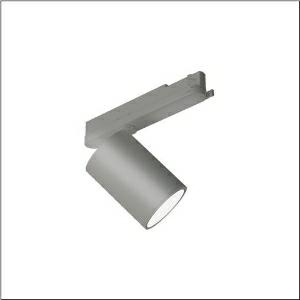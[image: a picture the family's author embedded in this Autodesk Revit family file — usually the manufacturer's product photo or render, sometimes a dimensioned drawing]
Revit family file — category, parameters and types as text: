
# Revit family: spot_31_51sf63mab4b
name_source: partatom
category: Lighting Fixtures
units: mm (PartAtom-declared; Revit-internal decimal feet)

## family parameters
Cut with Voids When Loaded = No
Host = Face
Light Source = No
Part Type = Normal
Room Calculation Point = No
Round Connector Dimension = Use Diameter
Shared = No

## types (1)
- --- (1 x LED, 5030 lm, 41.7 W, 3000K)
    Apparent Load = 42 VA
    CIE Flux Codes = 92 97 99 100 100
    Color Rendering = 90
    Color Temperature = 3000K
    Default Elevation = 1800 mm
    Description = Spot 31, directional spotlight, light control with lens, of PMMA, LED rated luminous flux: 4.830lm, light colour: 930, with 3-phase adapter, mains connection: 220..240V, AC, 50/60Hz, of aluminium, metallic grey (RAL 9006), length: 213mm, diameter: 90mm, protection rating (complete): IP20, insulation class (complete): insulation class I (protective earthing), certification: CE, impact resistance: IK02, permissible ambient temperature for indoor applications: -20..+40°C, packaging unit: 1 piece
    Height = 175 mm
    Lamp = 1 x LED
    Lamp Light Flux = 5030 lm
    Lamp Power = 41.7 W
    Lamp count = 1
    Length = 90 mm
    Luminous efficacy = 121 lm/W
    Manufacturer = Siteco
    ModVariant = No
    Model = 51SF63MAB4B
    Mounting Place = Ceiling
    Mounting Type = Pendant
    Number of Poles = 1
    OnlyDefault = Yes
    Power Factor = 1
    Product Name = Spot 31
    Product group = directional spotlight
    ProductGroupID = 906
    Protection Class = Protection class I
    Protection Degree = IP 20
    RLX_Detail_Level = 1
    RLX_Emergency_Light_Flux = 0 lm
    RLX_Emergency_Type = 0
    RLX_Emergency_Type_DB = No
    RlxData = <blob elided: 19973 chars, md5=6b2d84b3>
    Socket = socket
    Standby Power = 0 W
    System Light Flux = 5030 lm
    System Power = 42 W
    Type Comments = factory setting: luminous flux: 100 % | (ON | ON | ON | ON) | 1050 mA
    Type Image = l_1273725.jpg
    URL = http://relux.com
    VarID = @adj_146378
    Voltage = 0 V
    Weight = 0.00 kg
    Width = 0 mm  [stored 0 ft]

note: [stored X ft] marks values corroborated as IEEE doubles in the binary element streams (Revit-internal decimal feet)

## geometry (parser evidence)
native form markers: Blend x4, Sweep x9
no freeform markers — native parametric forms only
